# Revit family: Triple_Diverter_Trim-Grohe-29222_Series
name_source: partatom
category: Plumbing Fixtures
revit_build: Autodesk Revit 2018 (Build: 20170223_1515(x64)
units: mm (PartAtom-declared; Revit-internal decimal feet)

## family parameters
Cut with Voids When Loaded = No
Host = Face
OmniClass Number = 23.45.05.14.17
OmniClass Title = Showers
Part Type = Normal
Room Calculation Point = No
Round Connector Dimension = Use Diameter
Shared = Yes

## types (2) — shared parameters
Assembly Code = D2020300
CW Connection = Yes
CWFU = 3
Default Elevation = 0"
Description = 3-Way Diverter Trim
Flow rate = 1.75 gpm
HW Connection = Yes
HWFU = 3
Height = 4 1/2"
Installation Type = Wall Mounted
Length = 4 1/2"
Manufacturer = Grohe
Price = Prices may vary. Please consult Manufacturer Representative for most up-to-date price list.
Product Documentation Link = https://americanstandard.box.com
Product Page URL = https://www.grohe.us
URL = https://www.grohe.ca
Vent Connection = No
WFU = 4
Warranty Information = Limited lifetime Warranty
Waste Connection = No
Width = 2 3/16"

## per-type parameters (varying)
| type | Body Material | Material |
| 29222EN3 | Metal-Grohe-EN3-Brushed Nickel Infinity Finish | Metal-Grohe-EN3-Brushed_Nickel Infinity Finish |
| 29222003 | Metal-Grohe-003-Starlight Chrome | Metal-Grohe-003-Starlight Chrome |

note: column(s) folded — value = type name in every type: Model

## geometry (parser evidence)
native form markers: Sweep x3
no freeform markers — native parametric forms only
